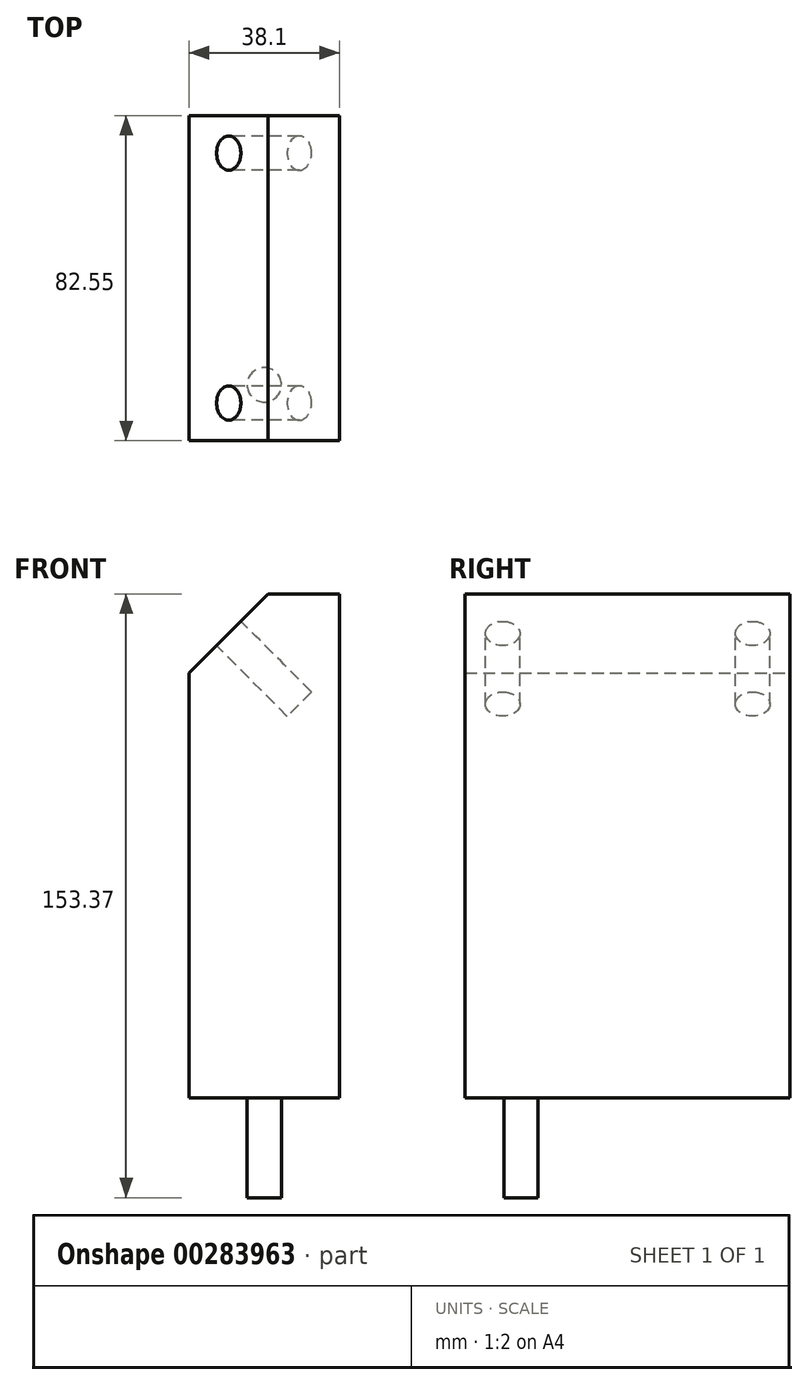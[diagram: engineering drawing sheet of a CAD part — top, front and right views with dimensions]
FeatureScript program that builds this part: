
annotation { "Feature Type Name" : "Feature", "Feature Type Description" : "" }
export const myFeature = defineFeature(function(context is Context, id is Id, definition is map)
    precondition{}
    {
        {
            var Q0;
            Q0=qCreatedBy(makeId("Front.planeOp"),FACE);
            var sketch = newSketch(context, id + "F0", { "sketchPlane" : qUnion([Q0])});
            skLineSegment(sketch, "E0", {"start": v(0, 0) * mm, "end": v(38.1, 0) * mm});
            skLineSegment(sketch, "E1.0", {"start": v(20.02, 153.37) * mm, "end": v(38.1, 153.37) * mm});
            skLineSegment(sketch, "E2", {"start": v(38.1, 0) * mm, "end": v(38.1, 153.37) * mm});
            skLineSegment(sketch, "E3", {"start": v(38.1, 153.37) * mm, "end": v(20.02, 153.37) * mm});
            skLineSegment(sketch, "E4", {"start": v(20.02, 153.37) * mm, "end": v(0, 133.35) * mm});
            skLineSegment(sketch, "E5", {"start": v(0, 0) * mm, "end": v(0, 133.35) * mm});
            skSolve(sketch);
        }
        {
            var Q0;
            Q0 = qSketchRegion(id + "F0", true);
            extrude(context, id + "F1", {"entities" : qUnion([Q0]), "depth" : 82.55 * mm});
        }
        {
            var Q0;
            Q0=makeQuery(id+"F1.opExtrude","SWEPT_FACE",FACE,{"disambiguationData":[OSD([sQuery(id+"F0.wireOp",EDGE,"E4")])]});
            var sketch = newSketch(context, id + "F2", { "sketchPlane" : qUnion([Q0])});
            skLineSegment(sketch, "E6.0", {"start": v(9.53, 108.45) * mm, "end": v(9.53, 105) * mm});
            skCircle(sketch, "E7", {"center": v(9.53, 108.45) * mm, "radius": 4.36 * mm});
            skCircle(sketch, "E8", {"center": v(73.03, 108.45) * mm, "radius": 4.36 * mm});
            skSolve(sketch);
        }
        {
            var Q0;
            Q0 = qSketchRegion(id + "F2", true);
            extrude(context, id + "F3", {"entities" : qUnion([Q0]), "operationType" : NewBodyOperationType.REMOVE, "oppositeDirection" : true, "depth" : 25.4 * mm});
        }
        {
            var Q0;
            Q0=makeQuery(id+"F1.opExtrude","SWEPT_FACE",FACE,{"disambiguationData":[OSD([sQuery(id+"F0.wireOp",EDGE,"E0")])]});
            var sketch = newSketch(context, id + "F4", { "sketchPlane" : qUnion([Q0])});
            skPoint(sketch, "E9.endSnap0", {"position": v(0, 41.28) * mm});
            skLineSegment(sketch, "E10", {"start": v(19.05, 0) * mm, "end": v(19.05, 14.15) * mm});
            skCircle(sketch, "E11", {"center": v(19.05, 14.15) * mm, "radius": 4.37 * mm});
            skCircle(sketch, "E12.MirrorC", {"center": v(19.05, 68.4) * mm, "radius": 4.37 * mm});
            skSolve(sketch);
        }
        {
            var Q0;
            Q0=makeQuery(id+"F4.imprint","IMPRINT",FACE,{"disambiguationData":[TD([[makeQuery(id+"F4.imprint","IMPRINT",EDGE,{"derivedFrom":sQuery(id+"F4.wireOp",EDGE,"E11")}),1.0]])]});
            var Q1;
            Q1=makeQuery(id+"F4.imprint","IMPRINT",FACE,{"disambiguationData":[TD([[makeQuery(id+"F4.imprint","IMPRINT",EDGE,{"derivedFrom":sQuery(id+"F4.wireOp",EDGE,"E12.MirrorC")}),-1.0]])]});
            extrude(context, id + "F5", {"entities" : qUnion([Q0, Q1]), "operationType" : NewBodyOperationType.REMOVE, "oppositeDirection" : true, "depth" : 25.4 * mm});
        }
    });
